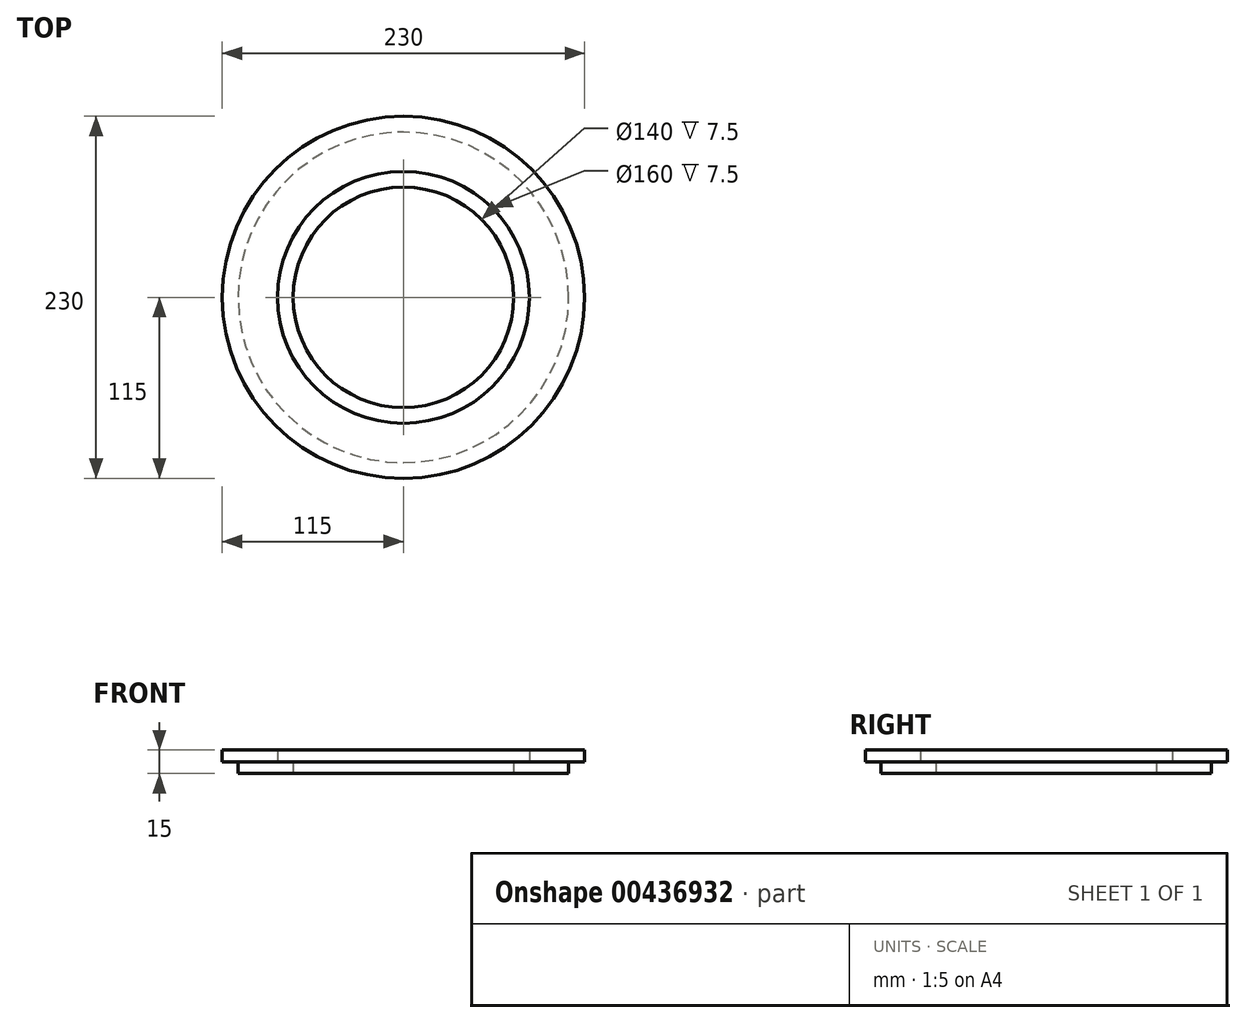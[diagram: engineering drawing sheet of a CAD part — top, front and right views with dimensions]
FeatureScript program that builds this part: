
annotation { "Feature Type Name" : "Feature", "Feature Type Description" : "" }
export const myFeature = defineFeature(function(context is Context, id is Id, definition is map)
    precondition{}
    {
        {
            var Q0;
            Q0=qCreatedBy(makeId("Front.planeOp"),FACE);
            var sketch = newSketch(context, id + "F0", { "sketchPlane" : qUnion([Q0])});
            skLineSegment(sketch, "E0", {"start": v(70, 0) * mm, "end": v(105, 0) * mm});
            skLineSegment(sketch, "E1", {"start": v(105, 0) * mm, "end": v(105, 7.5) * mm});
            skLineSegment(sketch, "E2", {"start": v(105, 7.5) * mm, "end": v(115, 7.5) * mm});
            skLineSegment(sketch, "E3", {"start": v(115, 7.5) * mm, "end": v(115, 15) * mm});
            skLineSegment(sketch, "E4", {"start": v(115, 15) * mm, "end": v(80, 15) * mm});
            skLineSegment(sketch, "E5", {"start": v(80, 15) * mm, "end": v(80, 7.5) * mm});
            skLineSegment(sketch, "E6", {"start": v(80, 7.5) * mm, "end": v(70, 7.5) * mm});
            skLineSegment(sketch, "E7", {"start": v(70, 7.5) * mm, "end": v(70, 0) * mm});
            skLineSegment(sketch, "E8", {"start": v(0, 0) * mm, "end": v(0, 115.63) * mm, "construction": true});
            skSolve(sketch);
        }
        {
            var Q0;
            Q0=makeQuery(id+"F0.imprint","IMPRINT",FACE,{"disambiguationData":[TD([[makeQuery(id+"F0.imprint","IMPRINT",EDGE,{"derivedFrom":sQuery(id+"F0.wireOp",EDGE,"E0")}),1.0]])]});
            var Q1;
            Q1=sQuery(id+"F0.wireOp",EDGE,"E8");
            var Q2;
            Q2=sQuery(id+"F0.wireOp",EDGE,"E8");
            revolve(context, id + "F1", {"entities" : qUnion([Q0]), "surfaceEntities" : qUnion([Q1]), "axis" : qUnion([Q2]), "revolveType" : RevolveType.FULL});
        }
    });
